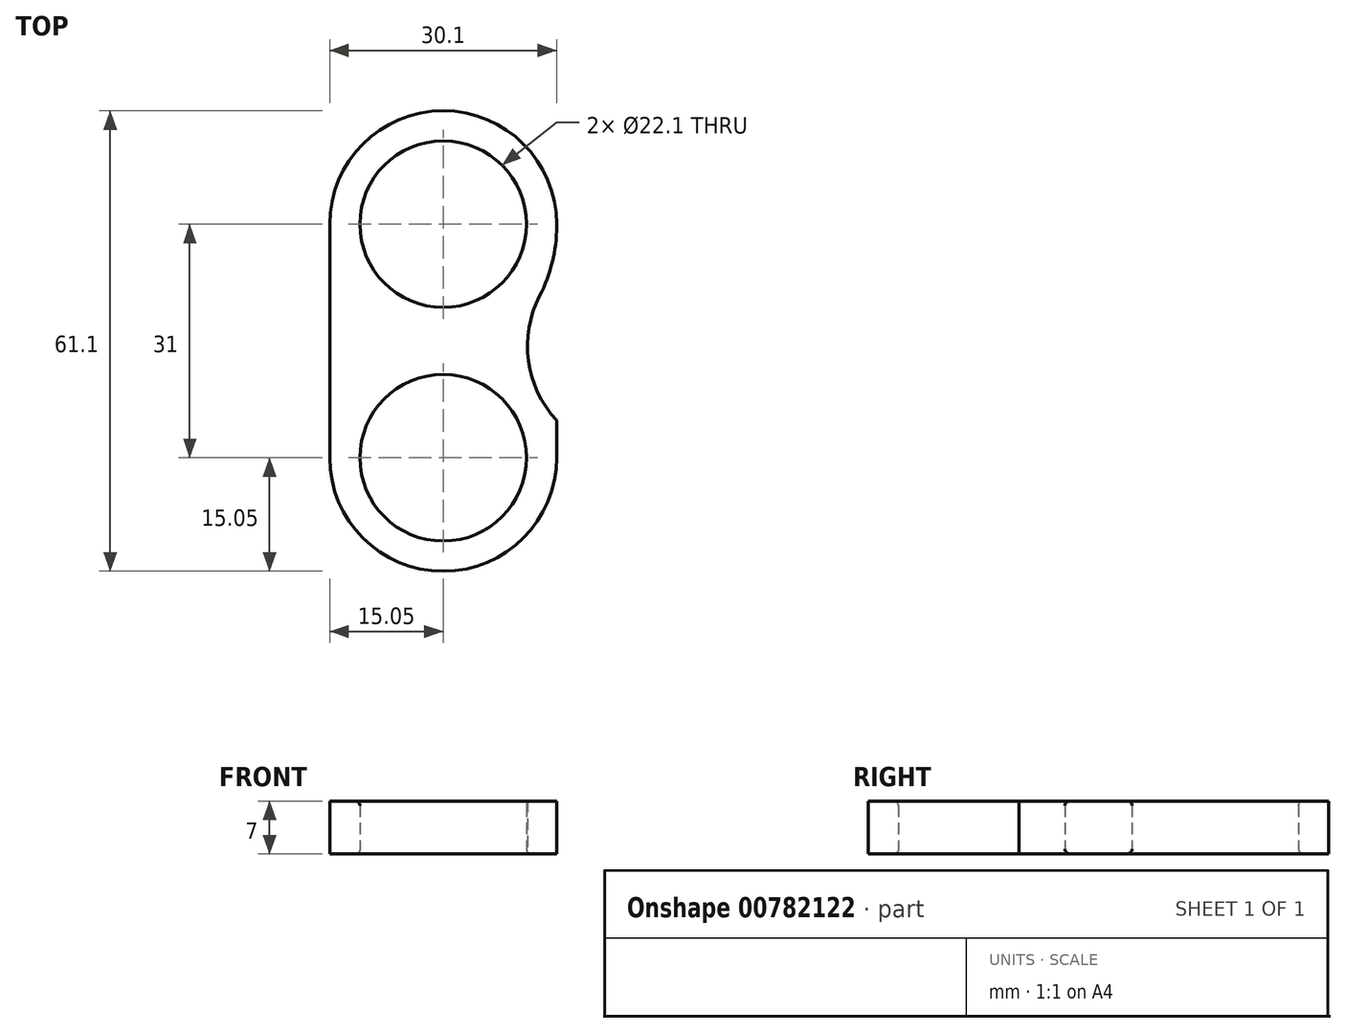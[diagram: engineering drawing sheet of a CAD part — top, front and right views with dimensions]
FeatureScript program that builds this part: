
annotation { "Feature Type Name" : "Feature", "Feature Type Description" : "" }
export const myFeature = defineFeature(function(context is Context, id is Id, definition is map)
    precondition{}
    {
        {
            var Q0;
            Q0=qCreatedBy(makeId("Top.planeOp"),FACE);
            var sketch = newSketch(context, id + "F0", { "sketchPlane" : qUnion([Q0])});
            skCircle(sketch, "E0", {"center": v(0, 0) * mm, "radius": 11.05 * mm});
            skCircle(sketch, "E1", {"center": v(0, 0) * mm, "radius": 15.05 * mm});
            skSolve(sketch);
        }
        {
            var Q0;
            Q0=qSketchRegion(id+"F0",true);
            extrude(context, id + "F1", {"entities" : qUnion([Q0]), "depth" : 7 * mm, "offsetDistance" : 25 * mm});
        }
        {
            var Q0;
            Q0=qCreatedBy(makeId("Top.planeOp"),FACE);
            var sketch = newSketch(context, id + "F2", { "sketchPlane" : qUnion([Q0])});
            skCircle(sketch, "E2", {"center": v(0, 31) * mm, "radius": 11.05 * mm});
            skArc(sketch, "E3", {"start": v(15.05, 31) * mm, "mid": v(0, 46.05) * mm, "end": v(-15.05, 31) * mm});
            skArc(sketch, "E4.0", {"start": v(15.05, 0) * mm, "mid": v(0, 15.05) * mm, "end": v(-15.05, 0) * mm});
            skLineSegment(sketch, "E5", {"start": v(0, 31) * mm, "end": v(-15.05, 31) * mm, "construction": true});
            skLineSegment(sketch, "E6", {"start": v(0, 31) * mm, "end": v(15.05, 31) * mm, "construction": true});
            skLineSegment(sketch, "E7", {"start": v(0, 0) * mm, "end": v(-15.05, 0) * mm, "construction": true});
            skLineSegment(sketch, "E8", {"start": v(0, 0) * mm, "end": v(15.05, 0) * mm, "construction": true});
            skLineSegment(sketch, "E9", {"start": v(-15.05, 31) * mm, "end": v(-15.05, 0) * mm});
            skLineSegment(sketch, "E10", {"start": v(15.05, 31) * mm, "end": v(15.05, 0) * mm});
            skSolve(sketch);
        }
        {
            var Q0;
            Q0=qSketchRegion(id+"F2",true);
            var Q1;
            Q1=makeQuery(id+"F1.opExtrude","CAP_FACE",FACE,{"disambiguationData":[OSD([sQuery(id+"F0.wireOp",EDGE,"E0"),sQuery(id+"F0.wireOp",EDGE,"E1")])],"isStart":false});
            extrude(context, id + "F3", {"entities" : qUnion([Q0]), "operationType" : NewBodyOperationType.ADD, "endBound" : BoundingType.UP_TO_SURFACE, "depth" : 25 * mm, "endBoundEntityFace" : qUnion([Q1]), "offsetDistance" : 25 * mm});
        }
        {
            var Q0;
            Q0=qCreatedBy(makeId("Top.planeOp"),FACE);
            var sketch = newSketch(context, id + "F4", { "sketchPlane" : qUnion([Q0])});
            skLineSegment(sketch, "E11.0", {"start": v(15.05, 24.69) * mm, "end": v(15.05, 8.69) * mm});
            skLineSegment(sketch, "E12.0", {"start": v(28.9, 0.69) * mm, "end": v(15.05, 8.69) * mm});
            skArc(sketch, "E13", {"start": v(15.05, 24.69) * mm, "mid": v(13.12, 7.58) * mm, "end": v(28.9, 0.69) * mm});
            skPoint(sketch, "E14.orphan", {"position": v(15.05, 31) * mm});
            skPoint(sketch, "E15.orphan", {"position": v(34.37, -2.47) * mm});
            skSolve(sketch);
        }
        {
            var Q0;
            Q0 = qSketchRegion(id + "F4", true);
            var Q1;
            {var subQ0=sQuery(id+"F2.wireOp",EDGE,"E10");var subQ1=sQuery(id+"F2.wireOp",EDGE,"E9");var subQ2=sQuery(id+"F2.wireOp",EDGE,"E4.0");var subQ3=sQuery(id+"F2.wireOp",EDGE,"E3");var subQ4=sQuery(id+"F2.wireOp",EDGE,"E2");Q1=makeQuery(id+"F0EbBsUhQH7FECo_1.2.F3.boolean.opBoolean","MERGE",FACE,{"derivedFrom":[makeQuery(id+"F0EbBsUhQH7FECo_1.1.F3.boolean.opBoolean","MERGE",FACE,{"derivedFrom":[makeQuery(id+"F3.boolean.opBoolean","MERGE",FACE,{"derivedFrom":[makeQuery(id+"F1.opExtrude","CAP_FACE",FACE,{"disambiguationData":[OSD([sQuery(id+"F0.wireOp",EDGE,"E0"),sQuery(id+"F0.wireOp",EDGE,"E1")])],"isStart":false}),makeQuery(id+"F3.opExtrude","CAP_FACE",FACE,{"disambiguationData":[OSD([subQ4,subQ3,subQ2,subQ1,subQ0])],"isStart":false})]}),makeQuery(id+"F0EbBsUhQH7FECo_1.1.F3.opExtrude","CAP_FACE",FACE,{"disambiguationData":[OSD([subQ4,subQ3,subQ2,subQ1,subQ0])],"isStart":false})]}),makeQuery(id+"F0EbBsUhQH7FECo_1.2.F3.opExtrude","CAP_FACE",FACE,{"disambiguationData":[OSD([subQ4,subQ3,subQ2,subQ1,subQ0])],"isStart":false})]});}
            extrude(context, id + "F5", {"entities" : qUnion([Q0]), "operationType" : NewBodyOperationType.REMOVE, "endBound" : BoundingType.UP_TO_SURFACE, "depth" : 25 * mm, "endBoundEntityFace" : qUnion([Q1]), "offsetDistance" : 25 * mm});
        }
        {
            var Q0;
            Q0=makeQuery(id+"F5.boolean.opBoolean","COPY",EDGE,{"derivedFrom":makeQuery(id+"F5.opExtrude","SWEPT_EDGE",EDGE,{"disambiguationData":[OSD([sQuery(id+"F4.wireOp",EDGE,"E11.0"),sQuery(id+"F4.wireOp",EDGE,"E13")])]})});
            var Q1;
            Q1=makeQuery(id+"FjNaIixI5rsmLLj_1.1.F5.boolean.opBoolean","COPY",EDGE,{"derivedFrom":makeQuery(id+"FjNaIixI5rsmLLj_1.1.F5.opExtrude","SWEPT_EDGE",EDGE,{"disambiguationData":[OSD([sQuery(id+"F4.wireOp",EDGE,"E12.0"),sQuery(id+"F4.wireOp",EDGE,"E13")])]})});
            var Q2;
            Q2=makeQuery(id+"F5.boolean.opBoolean","COPY",EDGE,{"derivedFrom":makeQuery(id+"F5.opExtrude","SWEPT_EDGE",EDGE,{"disambiguationData":[OSD([sQuery(id+"F4.wireOp",EDGE,"E12.0"),sQuery(id+"F4.wireOp",EDGE,"E13")])]})});
            var Q3;
            Q3=makeQuery(id+"FjNaIixI5rsmLLj_1.1.F5.boolean.opBoolean","COPY",EDGE,{"derivedFrom":makeQuery(id+"FjNaIixI5rsmLLj_1.1.F5.opExtrude","SWEPT_EDGE",EDGE,{"disambiguationData":[OSD([sQuery(id+"F4.wireOp",EDGE,"E11.0"),sQuery(id+"F4.wireOp",EDGE,"E13")])]})});
            var Q4;
            Q4=makeQuery(id+"FjNaIixI5rsmLLj_1.2.F5.boolean.opBoolean","COPY",EDGE,{"derivedFrom":makeQuery(id+"FjNaIixI5rsmLLj_1.2.F5.opExtrude","SWEPT_EDGE",EDGE,{"disambiguationData":[OSD([sQuery(id+"F4.wireOp",EDGE,"E12.0"),sQuery(id+"F4.wireOp",EDGE,"E13")])]})});
            var Q5;
            Q5=makeQuery(id+"FjNaIixI5rsmLLj_1.2.F5.boolean.opBoolean","COPY",EDGE,{"derivedFrom":makeQuery(id+"FjNaIixI5rsmLLj_1.2.F5.opExtrude","SWEPT_EDGE",EDGE,{"disambiguationData":[OSD([sQuery(id+"F4.wireOp",EDGE,"E11.0"),sQuery(id+"F4.wireOp",EDGE,"E13")])]})});
            fillet(context, id + "F6", {"entities" : qUnion([Q0, Q1, Q2, Q3, Q4, Q5]), "radius" : 20 * mm, "tangentPropagation" : true, "allowEdgeOverflow" : false});
        }
        {
            var Q0;
            Q0=makeQuery(id+"F0EbBsUhQH7FECo_1.1.F3.opExtrude","CAP_EDGE",EDGE,{"disambiguationData":[OSD([sQuery(id+"F2.wireOp",EDGE,"E9")])],"isStart":false});
            var Q1;
            Q1=makeQuery(id+"F0EbBsUhQH7FECo_1.1.F3.opExtrude","CAP_EDGE",EDGE,{"disambiguationData":[OSD([sQuery(id+"F2.wireOp",EDGE,"E9")])],"isStart":true});
            var Q2;
            Q2=makeQuery(id+"F3.opExtrude","CAP_EDGE",EDGE,{"disambiguationData":[OSD([sQuery(id+"F2.wireOp",EDGE,"E2")])],"isStart":false});
            var Q3;
            Q3=makeQuery(id+"F1.opExtrude","CAP_EDGE",EDGE,{"disambiguationData":[OSD([sQuery(id+"F0.wireOp",EDGE,"E0")])],"isStart":false});
            var Q4;
            Q4=makeQuery(id+"F0EbBsUhQH7FECo_1.1.F3.opExtrude","CAP_EDGE",EDGE,{"disambiguationData":[OSD([sQuery(id+"F2.wireOp",EDGE,"E2")])],"isStart":false});
            var Q5;
            Q5=makeQuery(id+"F0EbBsUhQH7FECo_1.2.F3.opExtrude","CAP_EDGE",EDGE,{"disambiguationData":[OSD([sQuery(id+"F2.wireOp",EDGE,"E2")])],"isStart":false});
            var Q6;
            Q6=makeQuery(id+"F0EbBsUhQH7FECo_1.1.F3.opExtrude","CAP_EDGE",EDGE,{"disambiguationData":[OSD([sQuery(id+"F2.wireOp",EDGE,"E2")])],"isStart":true});
            var Q7;
            Q7=makeQuery(id+"F1.opExtrude","CAP_EDGE",EDGE,{"disambiguationData":[OSD([sQuery(id+"F0.wireOp",EDGE,"E0")])],"isStart":true});
            var Q8;
            Q8=makeQuery(id+"F0EbBsUhQH7FECo_1.2.F3.opExtrude","CAP_EDGE",EDGE,{"disambiguationData":[OSD([sQuery(id+"F2.wireOp",EDGE,"E2")])],"isStart":true});
            var Q9;
            Q9=makeQuery(id+"F3.opExtrude","CAP_EDGE",EDGE,{"disambiguationData":[OSD([sQuery(id+"F2.wireOp",EDGE,"E2")])],"isStart":true});
            fillet(context, id + "F7", {"entities" : qUnion([Q0, Q1, Q2, Q3, Q4, Q5, Q6, Q7, Q8, Q9]), "radius" : .6 * mm, "tangentPropagation" : true, "allowEdgeOverflow" : false});
        }
    });
